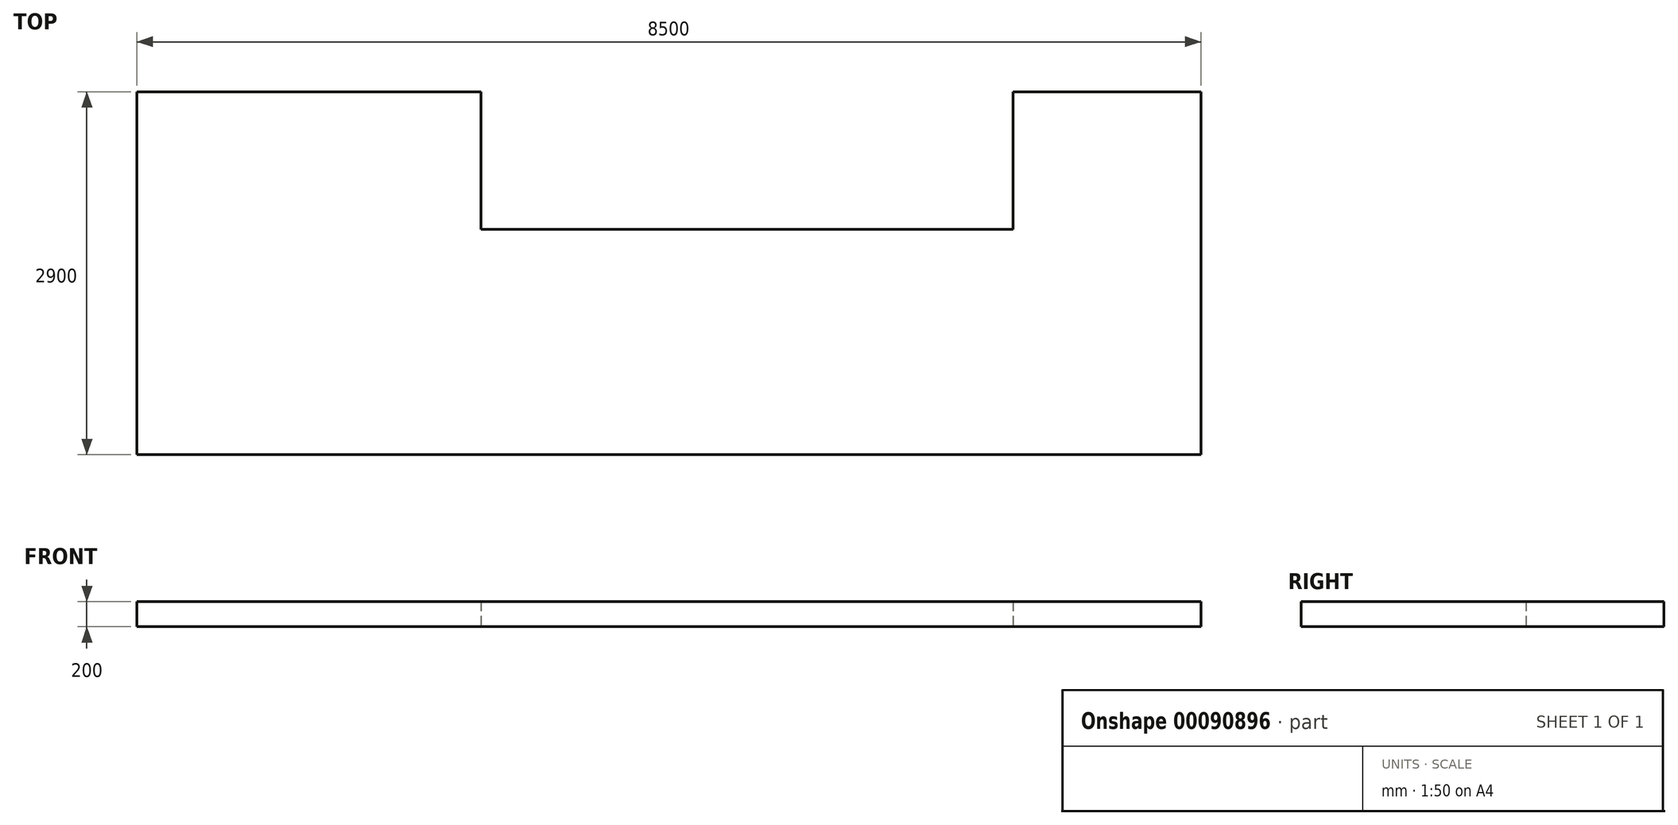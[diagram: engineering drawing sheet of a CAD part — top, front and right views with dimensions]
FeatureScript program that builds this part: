
annotation { "Feature Type Name" : "Feature", "Feature Type Description" : "" }
export const myFeature = defineFeature(function(context is Context, id is Id, definition is map)
    precondition{}
    {
        {
            var Q0;
            Q0=qCreatedBy(makeId("Top.planeOp"),FACE);
            var sketch = newSketch(context, id + "F0", { "sketchPlane" : qUnion([Q0])});
            skLineSegment(sketch, "E0.top", {"start": v(-5689.87, -1443.64) * mm, "end": v(2810.13, -1443.64) * mm});
            skLineSegment(sketch, "E0.left", {"start": v(-5689.87, 1456.36) * mm, "end": v(-5689.87, -1443.64) * mm});
            skLineSegment(sketch, "E0.right", {"start": v(2810.13, 1456.36) * mm, "end": v(2810.13, -1443.64) * mm});
            skLineSegment(sketch, "E1.top", {"start": v(1310.13, 356.36) * mm, "end": v(-2939.87, 356.36) * mm});
            skLineSegment(sketch, "E1.left", {"start": v(1310.13, 1456.36) * mm, "end": v(1310.13, 356.36) * mm});
            skLineSegment(sketch, "E1.right", {"start": v(-2939.87, 1456.36) * mm, "end": v(-2939.87, 356.36) * mm});
            skLineSegment(sketch, "E2", {"start": v(-5689.87, 1456.36) * mm, "end": v(-2939.87, 1456.36) * mm});
            skLineSegment(sketch, "E3", {"start": v(1310.13, 1456.36) * mm, "end": v(2810.13, 1456.36) * mm});
            skSolve(sketch);
        }
        {
            var Q0;
            Q0 = qSketchRegion(id + "F0", true);
            extrude(context, id + "F1", {"entities" : qUnion([Q0]), "depth" : 200 * mm});
        }
    });
